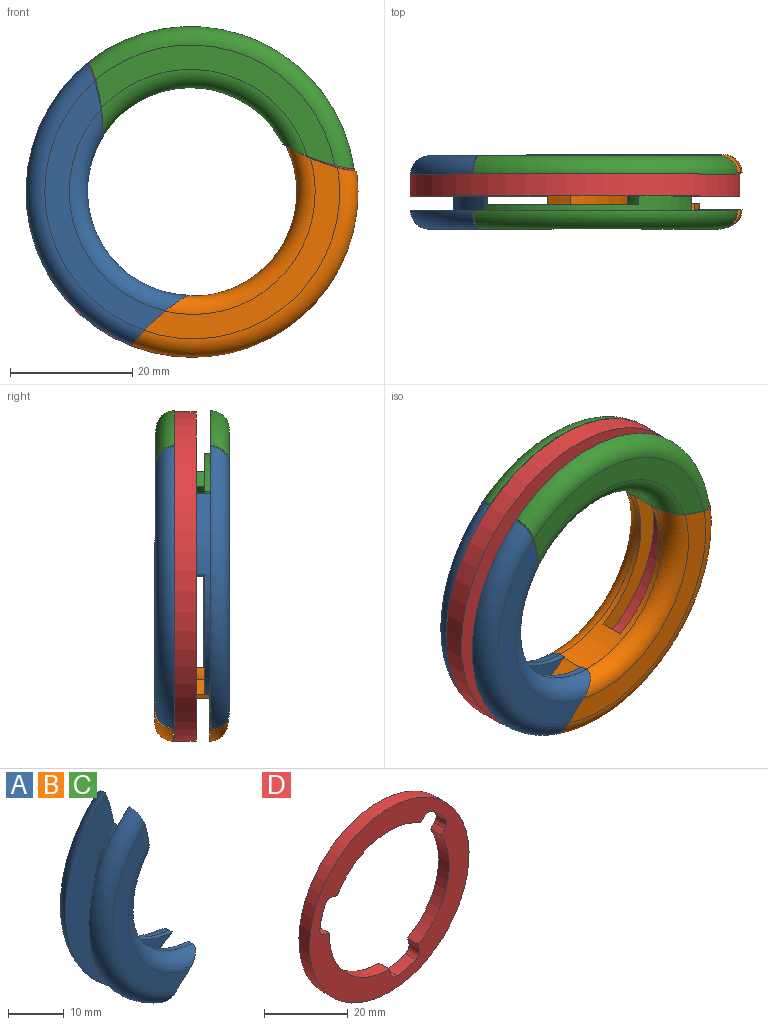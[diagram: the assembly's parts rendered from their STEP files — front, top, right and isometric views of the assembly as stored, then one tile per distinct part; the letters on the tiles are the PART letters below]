
ASSEMBLY  parts=4 mates=2
PART A: 16 faces, bbox 28.5x12x50.5 mm
  f0: cylinder r=20mm len=33.09mm, axis (0,1,0), area 142.1mm2, adj f1,f3,f4,f5,f7,f8,f9,f11
  f1: cylinder r=10mm len=4mm, axis (0,1,0), area 12.1mm2, adj f0,f2,f7,f11
  f2: cylinder r=17mm len=26.09mm, axis (0,1,0), area 109.6mm2, adj f1,f3,f5,f7,f9,f11,f12,f15
  f3: cylinder r=32mm len=12.09mm, axis (0,1,0), area 90.9mm2, adj f0,f2,f4,f6,f8,f10,f12,f13
  f4: plane 46.28x22.57mm, normal (0,-1,0), area 344.5mm2, adj f0,f3,f5,f14
  f5: cylinder r=32mm len=9.29mm, axis (0,-1,0), area 36.5mm2, adj f0,f2,f4,f6,f7,f14,f15
  f6: plane 40.84x19.57mm, normal (0,1,0), area 184.3mm2, adj f3,f5,f14,f15
  f7: plane 19.87x19.3mm, normal (0,-1,0), area 79.3mm2, adj f0,f1,f2,f5
  f8: plane 46.28x22.57mm, normal (0,1,0), area 344.5mm2, adj f0,f3,f9,f13
  f9: cylinder r=32mm len=9.29mm, axis (0,1,0), area 36.5mm2, adj f0,f2,f8,f10,f11,f12,f13
  f10: plane 40.84x19.57mm, normal (0,-1,0), area 184.3mm2, adj f3,f9,f12,f13
  f11: plane 19.87x19.3mm, normal (0,1,0), area 79.3mm2, adj f0,f1,f2,f9
  f12: torus R=20mm, axis (0,1,0), area 178.5mm2, adj f2,f3,f9,f10
  f13: torus R=24mm, axis (0,1,0), area 255.7mm2, adj f3,f8,f9,f10
  f14: torus R=24mm, axis (0,-1,0), area 255.7mm2, adj f3,f4,f5,f6
  f15: torus R=20mm, axis (0,-1,0), area 178.5mm2, adj f2,f3,f5,f6
PART B: same geometry as A
PART C: same geometry as A
PART D: 21 faces, bbox 54x3.6x54 mm
  f0: plane 54x54mm, normal (0,-1,0), area 894.9mm2, adj f2,f3,f4,f5,f6,f7,f8,f9
  f1: plane 54x54mm, normal (0,1,0), area 894.9mm2, adj f2,f3,f4,f5,f6,f7,f8,f9
  f2: cylinder r=20.3mm len=28.15mm, axis (0,1,0), area 116.7mm2, adj f0,f1,f9,f13
  f3: cylinder r=20.3mm len=28.02mm, axis (0,1,0), area 116.7mm2, adj f0,f1,f12,f14
  f4: cylinder r=27mm len=54mm, axis (0,1,0), area 610.7mm2, adj f0,f1
  f5: cylinder r=20.3mm len=20.75mm, axis (0,1,0), area 116.7mm2, adj f0,f1,f6,f10
  f6: plane 3.6x1.8mm, normal (0.97,0,0.25), area 6.7mm2, adj f0,f1,f5,f16
  f7: cylinder r=23.74mm len=6.34mm, axis (0,-1,0), area 23.7mm2, adj f0,f1,f15,f16
  f8: cylinder r=23.74mm len=4.68mm, axis (0,-1,0), area 23.7mm2, adj f0,f1,f17,f18
  f9: plane 3.6x1.33mm, normal (0.7,0,-0.71), area 6.7mm2, adj f0,f1,f2,f17
  f10: plane 3.6x1.79mm, normal (0.27,0,0.96), area 6.7mm2, adj f0,f1,f5,f20
  f11: cylinder r=23.74mm len=6.31mm, axis (0,-1,0), area 23.7mm2, adj f0,f1,f19,f20
  f12: plane 3.6x1.33mm, normal (-0.7,0,0.71), area 6.7mm2, adj f0,f1,f3,f18
  f13: plane 3.6x1.79mm, normal (-0.27,0,-0.96), area 6.7mm2, adj f0,f1,f2,f19
  f14: plane 3.6x1.8mm, normal (-0.97,0,-0.25), area 6.7mm2, adj f0,f1,f3,f15
  f15: cylinder r=2mm len=3.6mm, axis (0,-1,0), area 10.3mm2, adj f0,f1,f7,f14
  f16: cylinder r=2mm len=3.6mm, axis (0,-1,0), area 10.3mm2, adj f0,f1,f6,f7
  f17: cylinder r=2mm len=3.6mm, axis (0,-1,0), area 10.3mm2, adj f0,f1,f8,f9
  f18: cylinder r=2mm len=3.6mm, axis (0,-1,0), area 10.3mm2, adj f0,f1,f8,f12
  f19: cylinder r=2mm len=3.6mm, axis (0,-1,0), area 10.3mm2, adj f0,f1,f11,f13
  f20: cylinder r=2mm len=3.6mm, axis (0,-1,0), area 10.3mm2, adj f0,f1,f10,f11
PLACE A rot(axis=(0,-1,0),0.5deg) t=(-49.09,-0.01,8.07)mm
PLACE B rot(axis=(0,-1,0),118.9deg) t=(-48.82,0.19,7.92)mm
PLACE C rot(axis=(0,1,0),120.4deg) t=(-49.23,-0.01,8.03)mm
PLACE D t=(-49.17,0.19,7.92)mm fixed
MATE planar C.f4 <-> D.f11  axis (0,-1,0) through (-42.86,-0.01,26.52)mm
MATE planar D.f11 <-> A.f4  axis (0,1,0) through (-49.17,-0.01,7.92)mm
